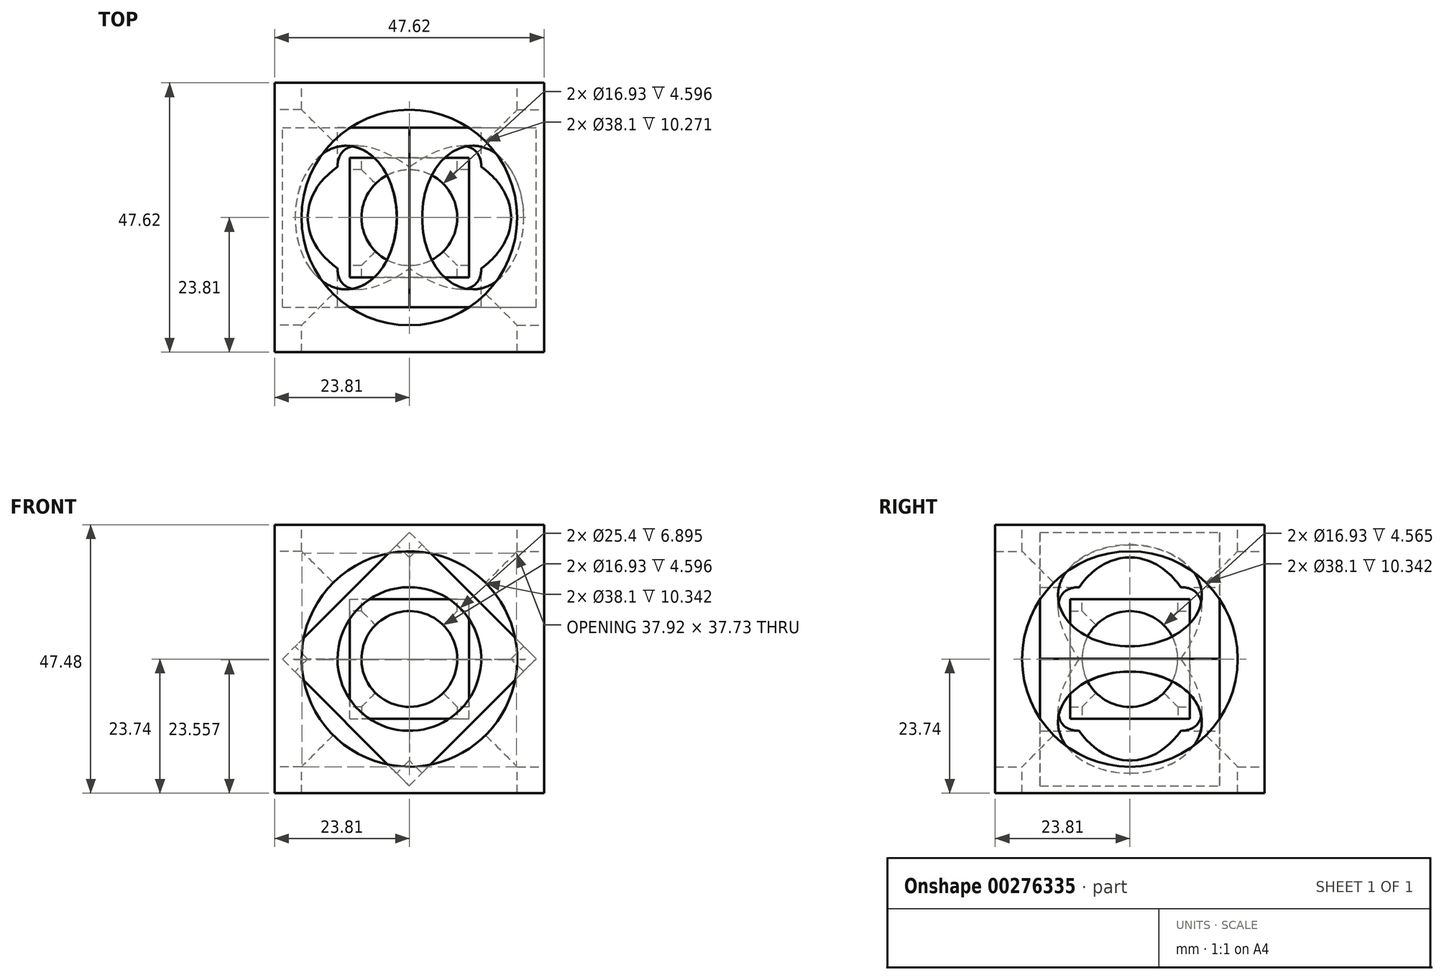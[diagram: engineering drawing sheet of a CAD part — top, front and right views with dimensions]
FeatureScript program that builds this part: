
annotation { "Feature Type Name" : "Feature", "Feature Type Description" : "" }
export const myFeature = defineFeature(function(context is Context, id is Id, definition is map)
    precondition{}
    {
        {
            var Q0;
            Q0=qCreatedBy(makeId("Front.planeOp"),FACE);
            var sketch = newSketch(context, id + "F0", { "sketchPlane" : qUnion([Q0])});
            skLineSegment(sketch, "E0.bottom", {"start": v(-7.94, 7.87) * mm, "end": v(7.94, 7.87) * mm});
            skLineSegment(sketch, "E0.top", {"start": v(-7.94, -7.87) * mm, "end": v(7.94, -7.87) * mm});
            skLineSegment(sketch, "E0.left", {"start": v(-7.94, 7.87) * mm, "end": v(-7.94, -7.87) * mm});
            skLineSegment(sketch, "E0.right", {"start": v(7.94, 7.87) * mm, "end": v(7.94, -7.87) * mm});
            skPoint(sketch, "E0.middle", {"position": v(0, 0) * mm});
            skLineSegment(sketch, "E1.bottom", {"start": v(-15.87, 15.38) * mm, "end": v(15.88, 15.38) * mm});
            skLineSegment(sketch, "E1.top", {"start": v(-15.88, -15.38) * mm, "end": v(15.87, -15.38) * mm});
            skLineSegment(sketch, "E1.left", {"start": v(-15.87, 15.38) * mm, "end": v(-15.88, -15.38) * mm});
            skLineSegment(sketch, "E1.right", {"start": v(15.88, 15.38) * mm, "end": v(15.87, -15.38) * mm});
            skLineSegment(sketch, "E2.bottom", {"start": v(-23.81, 23.74) * mm, "end": v(23.81, 23.74) * mm});
            skLineSegment(sketch, "E2.top", {"start": v(-23.81, -23.74) * mm, "end": v(23.81, -23.74) * mm});
            skLineSegment(sketch, "E2.left", {"start": v(-23.81, 23.74) * mm, "end": v(-23.81, -23.74) * mm});
            skLineSegment(sketch, "E2.right", {"start": v(23.81, 23.74) * mm, "end": v(23.81, -23.74) * mm});
            skCircle(sketch, "E3", {"center": v(0, 0) * mm, "radius": 4.65 * mm});
            skCircle(sketch, "E4", {"center": v(0, 0) * mm, "radius": 6.03 * mm});
            skCircle(sketch, "E5", {"center": v(0, 0) * mm, "radius": 4.76 * mm});
            skCircle(sketch, "E6", {"center": v(0, 0) * mm, "radius": 9.53 * mm});
            skCircle(sketch, "E7", {"center": v(0, 0) * mm, "radius": 11.75 * mm});
            skCircle(sketch, "E8", {"center": v(0, 0) * mm, "radius": 16.83 * mm});
            skCircle(sketch, "E9", {"center": v(0, 0) * mm, "radius": 19.05 * mm});
            skSolve(sketch);
        }
        {
            var Q0;
            Q0=makeQuery(id+"F0.imprint","IMPRINT",FACE,{"disambiguationData":[TD([[makeQuery(id+"F0.imprint","IMPRINT",EDGE,{"derivedFrom":sQuery(id+"F0.wireOp",EDGE,"E2.bottom")}),-1.0]])]});
            var Q1;
            {var subQ0=sQuery(id+"F0.wireOp",EDGE,"E1.left");var subQ1=sQuery(id+"F0.wireOp",EDGE,"E1.bottom");var subQ2=makeQuery(id+"F0.imprint","INTERSECT",VERTEX,{"derivedFrom":[subQ1,subQ0]});Q1=makeQuery(id+"F0.imprint","IMPRINT",FACE,{"disambiguationData":[TD([[makeQuery(id+"F0.imprint","IMPRINT",EDGE,{"disambiguationData":[TD([[subQ2,-1.0]])],"derivedFrom":subQ1}),-1.0]])]});}
            var Q2;
            {var subQ0=sQuery(id+"F0.wireOp",EDGE,"E1.right");var subQ1=sQuery(id+"F0.wireOp",EDGE,"E1.bottom");var subQ2=makeQuery(id+"F0.imprint","INTERSECT",VERTEX,{"derivedFrom":[subQ1,subQ0]});Q2=makeQuery(id+"F0.imprint","IMPRINT",FACE,{"disambiguationData":[TD([[makeQuery(id+"F0.imprint","IMPRINT",EDGE,{"disambiguationData":[TD([[subQ2,1.0]])],"derivedFrom":subQ1}),-1.0]])]});}
            var Q3;
            {var subQ0=sQuery(id+"F0.wireOp",EDGE,"E1.right");var subQ1=sQuery(id+"F0.wireOp",EDGE,"E1.top");var subQ2=makeQuery(id+"F0.imprint","INTERSECT",VERTEX,{"derivedFrom":[subQ1,subQ0]});Q3=makeQuery(id+"F0.imprint","IMPRINT",FACE,{"disambiguationData":[TD([[makeQuery(id+"F0.imprint","IMPRINT",EDGE,{"disambiguationData":[TD([[subQ2,1.0]])],"derivedFrom":subQ1}),1.0]])]});}
            var Q4;
            {var subQ0=sQuery(id+"F0.wireOp",EDGE,"E1.left");var subQ1=sQuery(id+"F0.wireOp",EDGE,"E1.top");var subQ2=makeQuery(id+"F0.imprint","INTERSECT",VERTEX,{"derivedFrom":[subQ1,subQ0]});Q4=makeQuery(id+"F0.imprint","IMPRINT",FACE,{"disambiguationData":[TD([[makeQuery(id+"F0.imprint","IMPRINT",EDGE,{"disambiguationData":[TD([[subQ2,-1.0]])],"derivedFrom":subQ1}),1.0]])]});}
            extrude(context, id + "F1", {"entities" : qUnion([Q0, Q1, Q2, Q3, Q4]), "endBound" : BoundingType.SYMMETRIC, "depth" : 47.62 * mm});
        }
        {
            var Q0;
            Q0=makeQuery(id+"F1.opExtrude","SWEPT_FACE",FACE,{"disambiguationData":[OSD([sQuery(id+"F0.wireOp",EDGE,"E2.bottom")])]});
            var sketch = newSketch(context, id + "F2", { "sketchPlane" : qUnion([Q0])});
            skPoint(sketch, "E10.middle", {"position": v(0, 0) * mm});
            skLineSegment(sketch, "E11.bottom", {"start": v(-23.81, 23.74) * mm, "end": v(23.81, 23.74) * mm});
            skLineSegment(sketch, "E11.top", {"start": v(-23.81, -23.74) * mm, "end": v(23.81, -23.74) * mm});
            skLineSegment(sketch, "E11.left", {"start": v(-23.81, 23.74) * mm, "end": v(-23.81, -23.74) * mm});
            skLineSegment(sketch, "E11.right", {"start": v(23.81, 23.74) * mm, "end": v(23.81, -23.74) * mm});
            skCircle(sketch, "E12", {"center": v(0, 0) * mm, "radius": 16.83 * mm});
            skCircle(sketch, "E13", {"center": v(0, 0) * mm, "radius": 19.05 * mm});
            skSolve(sketch);
        }
        {
            var Q0;
            Q0=makeQuery(id+"F2.imprint","IMPRINT",FACE,{"disambiguationData":[TD([[makeQuery(id+"F2.imprint","IMPRINT",EDGE,{"derivedFrom":sQuery(id+"F2.wireOp",EDGE,"E12")}),1.0]])]});
            var Q1;
            Q1=makeQuery(id+"F2.imprint","IMPRINT",FACE,{"disambiguationData":[TD([[makeQuery(id+"F2.imprint","IMPRINT",EDGE,{"derivedFrom":sQuery(id+"F2.wireOp",EDGE,"E12")}),-1.0]])]});
            extrude(context, id + "F3", {"entities" : qUnion([Q0, Q1]), "operationType" : NewBodyOperationType.REMOVE, "endBound" : BoundingType.SYMMETRIC, "oppositeDirection" : true, "depth" : 47.62 * mm});
        }
        {
            var Q0;
            Q0=makeQuery(id+"F1.opExtrude","SWEPT_FACE",FACE,{"disambiguationData":[OSD([sQuery(id+"F0.wireOp",EDGE,"E2.right")])]});
            var sketch = newSketch(context, id + "F4", { "sketchPlane" : qUnion([Q0])});
            skCircle(sketch, "E14", {"center": v(0, 0) * mm, "radius": 19.05 * mm});
            skSolve(sketch);
        }
        {
            var Q0;
            Q0=makeQuery(id+"F4.imprint","IMPRINT",FACE,{"disambiguationData":[TD([[makeQuery(id+"F4.imprint","IMPRINT",EDGE,{"derivedFrom":sQuery(id+"F4.wireOp",EDGE,"E14")}),1.0]])]});
            extrude(context, id + "F5", {"entities" : qUnion([Q0]), "operationType" : NewBodyOperationType.REMOVE, "oppositeDirection" : true, "depth" : 25.4 * mm});
        }
        {
            var Q0;
            Q0=makeQuery(id+"F1.opExtrude","SWEPT_FACE",FACE,{"disambiguationData":[OSD([sQuery(id+"F0.wireOp",EDGE,"E2.top")])]});
            var sketch = newSketch(context, id + "F6", { "sketchPlane" : qUnion([Q0])});
            skCircle(sketch, "E15", {"center": v(0, 0) * mm, "radius": 19.05 * mm});
            skSolve(sketch);
        }
        {
            var Q0;
            Q0=makeQuery(id+"F6.imprint","IMPRINT",FACE,{"disambiguationData":[TD([[makeQuery(id+"F6.imprint","IMPRINT",EDGE,{"derivedFrom":sQuery(id+"F6.wireOp",EDGE,"E15")}),1.0]])]});
            var Q1;
            Q1=makeQuery(id+"F1.opExtrude","SWEPT_BODY",BODY,{"disambiguationData":[OSD([sQuery(id+"F0.wireOp",EDGE,"E2.bottom"),sQuery(id+"F0.wireOp",EDGE,"E2.top"),sQuery(id+"F0.wireOp",EDGE,"E2.left"),sQuery(id+"F0.wireOp",EDGE,"E2.right"),sQuery(id+"F0.wireOp",EDGE,"E9")])]});
            extrude(context, id + "F7", {"entities" : qUnion([Q0]), "operationType" : NewBodyOperationType.REMOVE, "endBound" : BoundingType.UP_TO_BODY, "oppositeDirection" : true, "endBoundEntityBody" : qUnion([Q1]), "depth" : 25.4 * mm});
        }
        {
            var Q0;
            Q0=makeQuery(id+"F1.opExtrude","SWEPT_FACE",FACE,{"disambiguationData":[OSD([sQuery(id+"F0.wireOp",EDGE,"E2.left")])]});
            var sketch = newSketch(context, id + "F8", { "sketchPlane" : qUnion([Q0])});
            skCircle(sketch, "E16", {"center": v(0, 0) * mm, "radius": 19.05 * mm});
            skSolve(sketch);
        }
        {
            var Q0;
            Q0 = qSketchRegion(id + "F8", true);
            var Q1;
            Q1=makeQuery(id+"F1.opExtrude","SWEPT_BODY",BODY,{"disambiguationData":[OSD([sQuery(id+"F0.wireOp",EDGE,"E2.bottom"),sQuery(id+"F0.wireOp",EDGE,"E2.top"),sQuery(id+"F0.wireOp",EDGE,"E2.left"),sQuery(id+"F0.wireOp",EDGE,"E2.right"),sQuery(id+"F0.wireOp",EDGE,"E9")])]});
            extrude(context, id + "F9", {"entities" : qUnion([Q0]), "operationType" : NewBodyOperationType.REMOVE, "endBound" : BoundingType.SYMMETRIC, "oppositeDirection" : true, "endBoundEntityBody" : qUnion([Q1]), "depth" : 47.62 * mm});
        }
        {
            var Q0;
            Q0=makeQuery(id+"F1.opExtrude","SWEPT_BODY",BODY,{"disambiguationData":[OSD([sQuery(id+"F0.wireOp",EDGE,"E2.bottom"),sQuery(id+"F0.wireOp",EDGE,"E2.top"),sQuery(id+"F0.wireOp",EDGE,"E2.left"),sQuery(id+"F0.wireOp",EDGE,"E2.right"),sQuery(id+"F0.wireOp",EDGE,"E9")])]});
            var Q1;
            Q1=sQuery(id+"F0.wireOp",VERTEX,"E0.middle");
            transform(context, id + "F10", {"entities" : qUnion([Q0]), "transformType" : TransformType.SCALE_UNIFORMLY, "scale" : 2 / 3, "scalePoint" : qUnion([Q1]), "makeCopy" : true});
        }
        {
            var Q0;
            Q0=makeQuery(id+"F10.opPattern","COPY",BODY,{"derivedFrom":makeQuery(id+"F1.opExtrude","SWEPT_BODY",BODY,{"disambiguationData":[OSD([sQuery(id+"F0.wireOp",EDGE,"E2.bottom"),sQuery(id+"F0.wireOp",EDGE,"E2.top"),sQuery(id+"F0.wireOp",EDGE,"E2.left"),sQuery(id+"F0.wireOp",EDGE,"E2.right"),sQuery(id+"F0.wireOp",EDGE,"E9")])]}),"instanceName":"1"});
            var Q1;
            Q1=sQuery(id+"F0.wireOp",EDGE,"E7");
            var Q2;
            Q2=sQuery(id+"F0.wireOp",VERTEX,"E0.middle");
            transform(context, id + "F11", {"entities" : qUnion([Q0]), "transformType" : TransformType.ROTATION, "transformAxis" : qUnion([Q1]), "angle" : 45 * degree, "makeCopy" : true});
        }
        {
            var Q0;
            Q0=makeQuery(id+"F10.opPattern","COPY",BODY,{"derivedFrom":makeQuery(id+"F1.opExtrude","SWEPT_BODY",BODY,{"disambiguationData":[OSD([sQuery(id+"F0.wireOp",EDGE,"E2.bottom"),sQuery(id+"F0.wireOp",EDGE,"E2.top"),sQuery(id+"F0.wireOp",EDGE,"E2.left"),sQuery(id+"F0.wireOp",EDGE,"E2.right"),sQuery(id+"F0.wireOp",EDGE,"E9")])]}),"instanceName":"1"});
            deleteBodies(context, id + "F12", {"entities" : qUnion([Q0])});
        }
        {
            var Q0;
            Q0=makeQuery(id+"F11.opPattern","COPY",BODY,{"derivedFrom":makeQuery(id+"F10.opPattern","COPY",BODY,{"derivedFrom":makeQuery(id+"F1.opExtrude","SWEPT_BODY",BODY,{"disambiguationData":[OSD([sQuery(id+"F0.wireOp",EDGE,"E2.bottom"),sQuery(id+"F0.wireOp",EDGE,"E2.top"),sQuery(id+"F0.wireOp",EDGE,"E2.left"),sQuery(id+"F0.wireOp",EDGE,"E2.right"),sQuery(id+"F0.wireOp",EDGE,"E9")])]}),"instanceName":"1"}),"instanceName":"1"});
            var Q1;
            Q1=sQuery(id+"F0.wireOp",VERTEX,"E0.middle");
            transform(context, id + "F13", {"entities" : qUnion([Q0]), "transformType" : TransformType.SCALE_UNIFORMLY, "scale" : 2 / 3, "scalePoint" : qUnion([Q1]), "makeCopy" : true});
        }
        {
            var Q0;
            Q0=makeQuery(id+"F13.opPattern","COPY",BODY,{"derivedFrom":makeQuery(id+"F11.opPattern","COPY",BODY,{"derivedFrom":makeQuery(id+"F10.opPattern","COPY",BODY,{"derivedFrom":makeQuery(id+"F1.opExtrude","SWEPT_BODY",BODY,{"disambiguationData":[OSD([sQuery(id+"F0.wireOp",EDGE,"E2.bottom"),sQuery(id+"F0.wireOp",EDGE,"E2.top"),sQuery(id+"F0.wireOp",EDGE,"E2.left"),sQuery(id+"F0.wireOp",EDGE,"E2.right"),sQuery(id+"F0.wireOp",EDGE,"E9")])]}),"instanceName":"1"}),"instanceName":"1"}),"instanceName":"1"});
            var Q1;
            Q1=sQuery(id+"F0.wireOp",EDGE,"E9");
            transform(context, id + "F14", {"entities" : qUnion([Q0]), "transformType" : TransformType.ROTATION, "transformAxis" : qUnion([Q1]), "angle" : 45 * degree, "makeCopy" : true});
        }
        {
            var Q0;
            Q0=makeQuery(id+"F13.opPattern","COPY",BODY,{"derivedFrom":makeQuery(id+"F11.opPattern","COPY",BODY,{"derivedFrom":makeQuery(id+"F10.opPattern","COPY",BODY,{"derivedFrom":makeQuery(id+"F1.opExtrude","SWEPT_BODY",BODY,{"disambiguationData":[OSD([sQuery(id+"F0.wireOp",EDGE,"E2.bottom"),sQuery(id+"F0.wireOp",EDGE,"E2.top"),sQuery(id+"F0.wireOp",EDGE,"E2.left"),sQuery(id+"F0.wireOp",EDGE,"E2.right"),sQuery(id+"F0.wireOp",EDGE,"E9")])]}),"instanceName":"1"}),"instanceName":"1"}),"instanceName":"1"});
            deleteBodies(context, id + "F15", {"entities" : qUnion([Q0])});
        }
        {
            var Q0;
            Q0=makeQuery(id+"F14.opPattern","COPY",BODY,{"derivedFrom":makeQuery(id+"F13.opPattern","COPY",BODY,{"derivedFrom":makeQuery(id+"F11.opPattern","COPY",BODY,{"derivedFrom":makeQuery(id+"F10.opPattern","COPY",BODY,{"derivedFrom":makeQuery(id+"F1.opExtrude","SWEPT_BODY",BODY,{"disambiguationData":[OSD([sQuery(id+"F0.wireOp",EDGE,"E2.bottom"),sQuery(id+"F0.wireOp",EDGE,"E2.top"),sQuery(id+"F0.wireOp",EDGE,"E2.left"),sQuery(id+"F0.wireOp",EDGE,"E2.right"),sQuery(id+"F0.wireOp",EDGE,"E9")])]}),"instanceName":"1"}),"instanceName":"1"}),"instanceName":"1"}),"instanceName":"1"});
            var Q1;
            Q1=sQuery(id+"F0.wireOp",VERTEX,"E0.middle");
            transform(context, id + "F16", {"entities" : qUnion([Q0]), "transformType" : TransformType.SCALE_UNIFORMLY, "scale" : 2 / 3, "scalePoint" : qUnion([Q1]), "makeCopy" : true});
        }
        {
            var Q0;
            Q0=makeQuery(id+"F16.opPattern","COPY",BODY,{"derivedFrom":makeQuery(id+"F14.opPattern","COPY",BODY,{"derivedFrom":makeQuery(id+"F13.opPattern","COPY",BODY,{"derivedFrom":makeQuery(id+"F11.opPattern","COPY",BODY,{"derivedFrom":makeQuery(id+"F10.opPattern","COPY",BODY,{"derivedFrom":makeQuery(id+"F1.opExtrude","SWEPT_BODY",BODY,{"disambiguationData":[OSD([sQuery(id+"F0.wireOp",EDGE,"E2.bottom"),sQuery(id+"F0.wireOp",EDGE,"E2.top"),sQuery(id+"F0.wireOp",EDGE,"E2.left"),sQuery(id+"F0.wireOp",EDGE,"E2.right"),sQuery(id+"F0.wireOp",EDGE,"E9")])]}),"instanceName":"1"}),"instanceName":"1"}),"instanceName":"1"}),"instanceName":"1"}),"instanceName":"1"});
            var Q1;
            Q1=sQuery(id+"F0.wireOp",EDGE,"E9");
            transform(context, id + "F17", {"entities" : qUnion([Q0]), "transformType" : TransformType.ROTATION, "transformAxis" : qUnion([Q1]), "angle" : 45 * degree, "makeCopy" : false});
        }
        {
            var Q0;
            Q0=makeQuery(id+"F16.opPattern","COPY",BODY,{"derivedFrom":makeQuery(id+"F14.opPattern","COPY",BODY,{"derivedFrom":makeQuery(id+"F13.opPattern","COPY",BODY,{"derivedFrom":makeQuery(id+"F11.opPattern","COPY",BODY,{"derivedFrom":makeQuery(id+"F10.opPattern","COPY",BODY,{"derivedFrom":makeQuery(id+"F1.opExtrude","SWEPT_BODY",BODY,{"disambiguationData":[OSD([sQuery(id+"F0.wireOp",EDGE,"E2.bottom"),sQuery(id+"F0.wireOp",EDGE,"E2.top"),sQuery(id+"F0.wireOp",EDGE,"E2.left"),sQuery(id+"F0.wireOp",EDGE,"E2.right"),sQuery(id+"F0.wireOp",EDGE,"E9")])]}),"instanceName":"1"}),"instanceName":"1"}),"instanceName":"1"}),"instanceName":"1"}),"instanceName":"1"});
            var Q1;
            Q1=sQuery(id+"F0.wireOp",VERTEX,"E0.middle");
            transform(context, id + "F18", {"entities" : qUnion([Q0]), "transformType" : TransformType.SCALE_UNIFORMLY, "scale" : 2 / 3, "scalePoint" : qUnion([Q1]), "makeCopy" : true});
        }
        {
            var Q0;
            Q0=makeQuery(id+"F18.opPattern","COPY",BODY,{"derivedFrom":makeQuery(id+"F16.opPattern","COPY",BODY,{"derivedFrom":makeQuery(id+"F14.opPattern","COPY",BODY,{"derivedFrom":makeQuery(id+"F13.opPattern","COPY",BODY,{"derivedFrom":makeQuery(id+"F11.opPattern","COPY",BODY,{"derivedFrom":makeQuery(id+"F10.opPattern","COPY",BODY,{"derivedFrom":makeQuery(id+"F1.opExtrude","SWEPT_BODY",BODY,{"disambiguationData":[OSD([sQuery(id+"F0.wireOp",EDGE,"E2.bottom"),sQuery(id+"F0.wireOp",EDGE,"E2.top"),sQuery(id+"F0.wireOp",EDGE,"E2.left"),sQuery(id+"F0.wireOp",EDGE,"E2.right"),sQuery(id+"F0.wireOp",EDGE,"E9")])]}),"instanceName":"1"}),"instanceName":"1"}),"instanceName":"1"}),"instanceName":"1"}),"instanceName":"1"}),"instanceName":"1"});
            var Q1;
            Q1=sQuery(id+"F0.wireOp",EDGE,"E8");
            transform(context, id + "F19", {"entities" : qUnion([Q0]), "transformType" : TransformType.ROTATION, "transformAxis" : qUnion([Q1]), "angle" : 45 * degree, "makeCopy" : false});
        }
        {
            var Q0;
            Q0=makeQuery(id+"F18.opPattern","COPY",BODY,{"derivedFrom":makeQuery(id+"F16.opPattern","COPY",BODY,{"derivedFrom":makeQuery(id+"F14.opPattern","COPY",BODY,{"derivedFrom":makeQuery(id+"F13.opPattern","COPY",BODY,{"derivedFrom":makeQuery(id+"F11.opPattern","COPY",BODY,{"derivedFrom":makeQuery(id+"F10.opPattern","COPY",BODY,{"derivedFrom":makeQuery(id+"F1.opExtrude","SWEPT_BODY",BODY,{"disambiguationData":[OSD([sQuery(id+"F0.wireOp",EDGE,"E2.bottom"),sQuery(id+"F0.wireOp",EDGE,"E2.top"),sQuery(id+"F0.wireOp",EDGE,"E2.left"),sQuery(id+"F0.wireOp",EDGE,"E2.right"),sQuery(id+"F0.wireOp",EDGE,"E9")])]}),"instanceName":"1"}),"instanceName":"1"}),"instanceName":"1"}),"instanceName":"1"}),"instanceName":"1"}),"instanceName":"1"});
            deleteBodies(context, id + "F20", {"entities" : qUnion([Q0])});
        }
        {
            var Q0;
            Q0=makeQuery(id+"F16.opPattern","COPY",BODY,{"derivedFrom":makeQuery(id+"F14.opPattern","COPY",BODY,{"derivedFrom":makeQuery(id+"F13.opPattern","COPY",BODY,{"derivedFrom":makeQuery(id+"F11.opPattern","COPY",BODY,{"derivedFrom":makeQuery(id+"F10.opPattern","COPY",BODY,{"derivedFrom":makeQuery(id+"F1.opExtrude","SWEPT_BODY",BODY,{"disambiguationData":[OSD([sQuery(id+"F0.wireOp",EDGE,"E2.bottom"),sQuery(id+"F0.wireOp",EDGE,"E2.top"),sQuery(id+"F0.wireOp",EDGE,"E2.left"),sQuery(id+"F0.wireOp",EDGE,"E2.right"),sQuery(id+"F0.wireOp",EDGE,"E9")])]}),"instanceName":"1"}),"instanceName":"1"}),"instanceName":"1"}),"instanceName":"1"}),"instanceName":"1"});
            deleteBodies(context, id + "F21", {"entities" : qUnion([Q0])});
        }
    });
